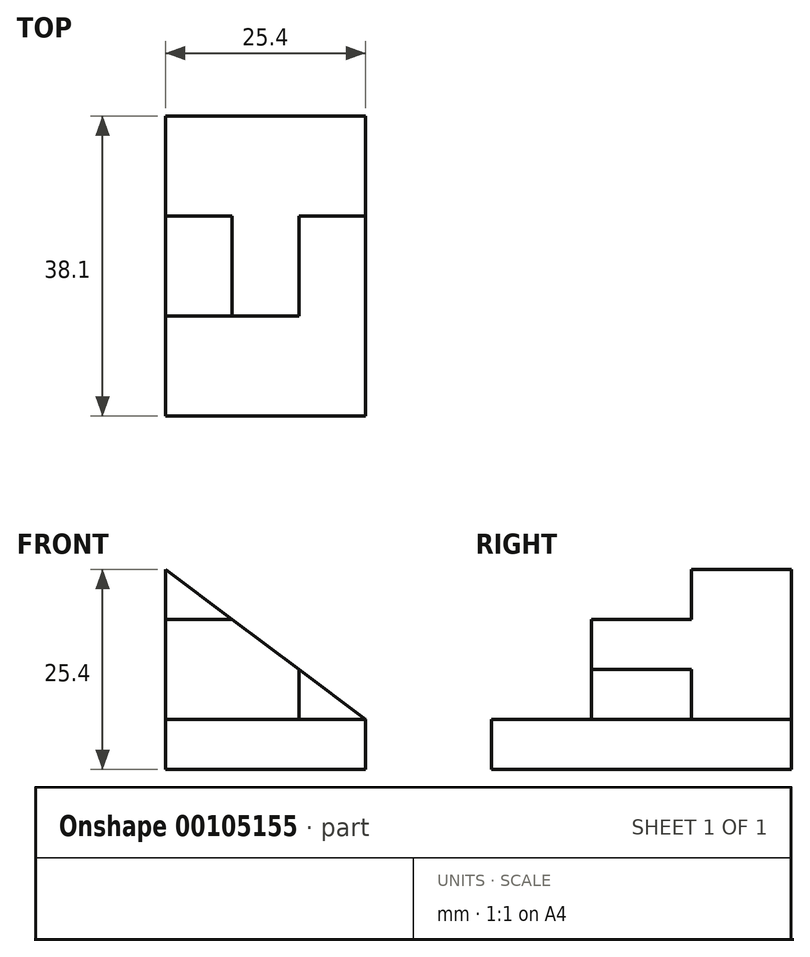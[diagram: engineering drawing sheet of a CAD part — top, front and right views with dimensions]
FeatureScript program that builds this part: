
annotation { "Feature Type Name" : "Feature", "Feature Type Description" : "" }
export const myFeature = defineFeature(function(context is Context, id is Id, definition is map)
    precondition{}
    {
        {
            var Q0;
            Q0=qCreatedBy(makeId("Front.planeOp"),FACE);
            var sketch = newSketch(context, id + "F0", { "sketchPlane" : qUnion([Q0])});
            skLineSegment(sketch, "E0", {"start": v(0, 25.4) * mm, "end": v(0, 0) * mm});
            skLineSegment(sketch, "E1", {"start": v(0, 0) * mm, "end": v(25.4, 0) * mm});
            skLineSegment(sketch, "E2", {"start": v(25.4, 0) * mm, "end": v(25.4, 6.35) * mm});
            skLineSegment(sketch, "E3", {"start": v(25.4, 6.35) * mm, "end": v(0, 25.4) * mm});
            skLineSegment(sketch, "E4", {"start": v(25.4, 6.35) * mm, "end": v(0, 6.35) * mm});
            skSolve(sketch);
        }
        {
            var Q0;
            Q0 = qSketchRegion(id + "F0", true);
            var Q1;
            Q1 = qSketchRegion(id + "Fer4LvhQJjPTqpZ_1", true);
            extrude(context, id + "F1", {"entities" : qUnion([Q0, Q1]), "depth" : 38.1 * mm});
        }
        {
            var Q0;
            Q0=makeQuery(id+"F1.opExtrude","SWEPT_FACE",FACE,{"disambiguationData":[OSD([sQuery(id+"F0.wireOp",EDGE,"E0")])]});
            var sketch = newSketch(context, id + "F2", { "sketchPlane" : qUnion([Q0])});
            skLineSegment(sketch, "E5.bottom", {"start": v(12.7, 25.4) * mm, "end": v(38.1, 25.4) * mm});
            skLineSegment(sketch, "E5.top", {"start": v(12.7, 19.05) * mm, "end": v(38.1, 19.05) * mm});
            skLineSegment(sketch, "E5.left", {"start": v(12.7, 25.4) * mm, "end": v(12.7, 19.05) * mm});
            skLineSegment(sketch, "E5.right", {"start": v(38.1, 25.4) * mm, "end": v(38.1, 19.05) * mm});
            skSolve(sketch);
        }
        {
            var Q0;
            Q0=makeQuery(id+"F2.imprint","IMPRINT",FACE,{"disambiguationData":[TD([[makeQuery(id+"F2.imprint","IMPRINT",EDGE,{"derivedFrom":sQuery(id+"F2.wireOp",EDGE,"E5.bottom")}),1.0]])]});
            extrude(context, id + "F3", {"entities" : qUnion([Q0]), "operationType" : NewBodyOperationType.REMOVE, "endBound" : BoundingType.THROUGH_ALL, "oppositeDirection" : true, "depth" : 25.4 * mm});
        }
        {
            var Q0;
            Q0=makeQuery(id+"F1.opExtrude","CAP_FACE",FACE,{"disambiguationData":[OSD([sQuery(id+"F0.wireOp",EDGE,"E0"),sQuery(id+"F0.wireOp",EDGE,"E1"),sQuery(id+"F0.wireOp",EDGE,"E2"),sQuery(id+"F0.wireOp",EDGE,"E3")])],"isStart":false});
            var sketch = newSketch(context, id + "F4", { "sketchPlane" : qUnion([Q0])});
            skLineSegment(sketch, "E6", {"start": v(25.4, 6.35) * mm, "end": v(16.93, 6.35) * mm});
            skLineSegment(sketch, "E7", {"start": v(16.93, 6.35) * mm, "end": v(16.93, 12.7) * mm});
            skSolve(sketch);
        }
        {
            var Q0;
            {var subQ0=sQuery(id+"F4.wireOp",EDGE,"E6");Q0=makeQuery(id+"F4.imprint","IMPRINT",FACE,{"disambiguationData":[TD([[makeQuery(id+"F4.imprint","IMPRINT",EDGE,{"derivedFrom":subQ0}),-1.0]])]});}
            extrude(context, id + "F5", {"entities" : qUnion([Q0]), "operationType" : NewBodyOperationType.REMOVE, "oppositeDirection" : true, "depth" : 25.4 * mm});
        }
        {
            var Q0;
            Q0=makeQuery(id+"F1.opExtrude","SWEPT_FACE",FACE,{"disambiguationData":[OSD([sQuery(id+"F0.wireOp",EDGE,"E0")])]});
            var sketch = newSketch(context, id + "F6", { "sketchPlane" : qUnion([Q0])});
            skLineSegment(sketch, "E8.bottom", {"start": v(38.1, 19.05) * mm, "end": v(25.4, 19.05) * mm});
            skLineSegment(sketch, "E8.top", {"start": v(38.1, 12.7) * mm, "end": v(25.4, 12.7) * mm});
            skLineSegment(sketch, "E8.left", {"start": v(38.1, 19.05) * mm, "end": v(38.1, 12.7) * mm});
            skLineSegment(sketch, "E8.right", {"start": v(25.4, 19.05) * mm, "end": v(25.4, 12.7) * mm});
            skSolve(sketch);
        }
        {
            var Q0;
            Q0=makeQuery(id+"F6.imprint","IMPRINT",FACE,{"disambiguationData":[TD([[makeQuery(id+"F6.imprint","IMPRINT",EDGE,{"derivedFrom":sQuery(id+"F6.wireOp",EDGE,"E8.bottom")}),-1.0]])]});
            extrude(context, id + "F7", {"entities" : qUnion([Q0]), "operationType" : NewBodyOperationType.REMOVE, "endBound" : BoundingType.THROUGH_ALL, "oppositeDirection" : true, "depth" : 25.4 * mm});
        }
        {
            var Q0;
            Q0=makeQuery(id+"F1.opExtrude","SWEPT_FACE",FACE,{"disambiguationData":[OSD([sQuery(id+"F0.wireOp",EDGE,"E0")])]});
            var sketch = newSketch(context, id + "F8", { "sketchPlane" : qUnion([Q0])});
            skLineSegment(sketch, "E9.bottom", {"start": v(25.4, 12.7) * mm, "end": v(38.1, 12.7) * mm});
            skLineSegment(sketch, "E9.top", {"start": v(25.4, 6.35) * mm, "end": v(38.1, 6.35) * mm});
            skLineSegment(sketch, "E9.left", {"start": v(25.4, 12.7) * mm, "end": v(25.4, 6.35) * mm});
            skLineSegment(sketch, "E9.right", {"start": v(38.1, 12.7) * mm, "end": v(38.1, 6.35) * mm});
            skSolve(sketch);
        }
        {
            var Q0;
            Q0=makeQuery(id+"F8.imprint","IMPRINT",FACE,{"disambiguationData":[TD([[makeQuery(id+"F8.imprint","IMPRINT",EDGE,{"derivedFrom":sQuery(id+"F8.wireOp",EDGE,"E9.bottom")}),1.0]])]});
            extrude(context, id + "F9", {"entities" : qUnion([Q0]), "operationType" : NewBodyOperationType.REMOVE, "endBound" : BoundingType.THROUGH_ALL, "oppositeDirection" : true, "depth" : 25.4 * mm});
        }
    });
